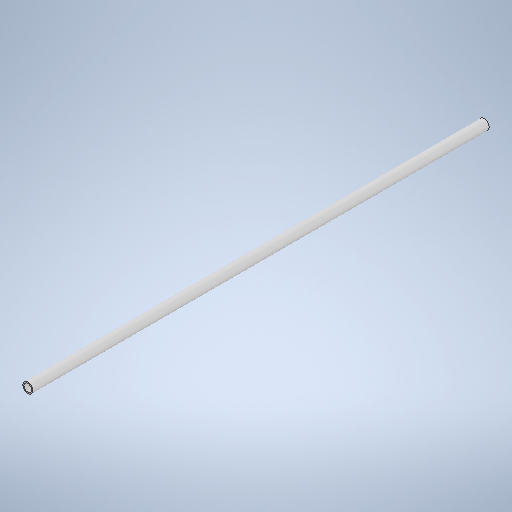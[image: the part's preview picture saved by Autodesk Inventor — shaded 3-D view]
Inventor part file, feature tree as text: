
AUTODESK INVENTOR PART (.ipt)
format: ipt  version: 2025 (Build 290162000, 162)  size: 252,928 bytes
history: native  units: in
note: dims shown in document units (in); Inventor stores cm internally (conversion verified against a paired STEP export)
features: extrude x1, sketch x1
ambient origin geometry x8: Origin, YZ Plane, XZ Plane, XY Plane, X Axis, Y Axis, Z Axis, Center Point
bodies: Solid1 (feature_tree)
feature tree (2):
  extrude  "Extrusion1"  Depth=48.0in
  sketch  "Sketch1"  dims[d0=1.04in d1=0.8in d2=48.0in d3=0.0in]
